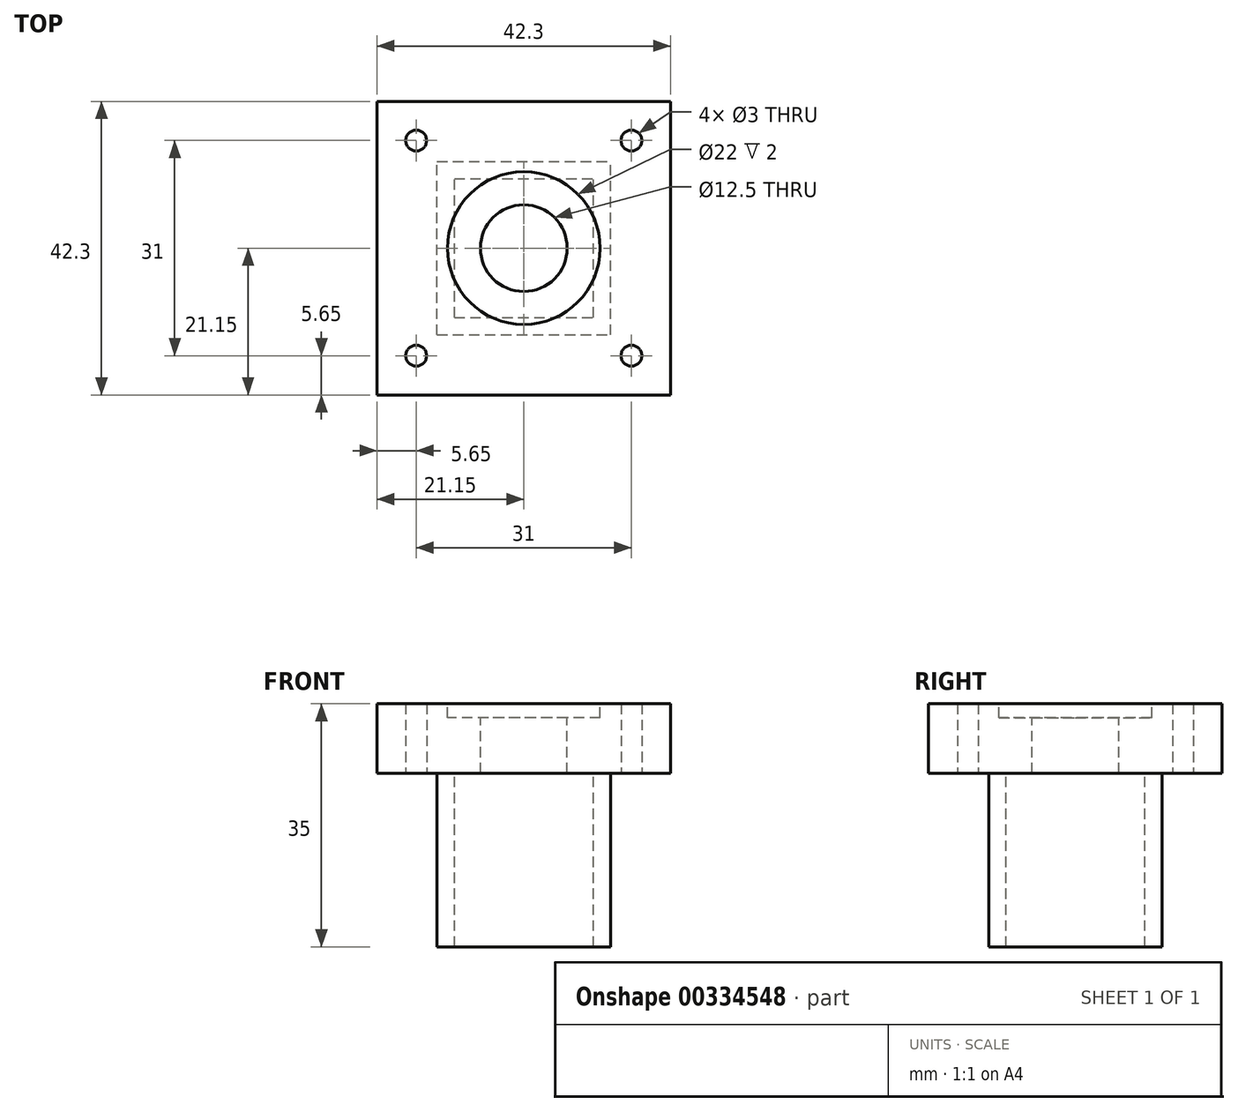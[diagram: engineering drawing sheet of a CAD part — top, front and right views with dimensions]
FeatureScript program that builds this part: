
annotation { "Feature Type Name" : "Feature", "Feature Type Description" : "" }
export const myFeature = defineFeature(function(context is Context, id is Id, definition is map)
    precondition{}
    {
        {
            var Q0;
            Q0=qCreatedBy(makeId("Top.planeOp"),FACE);
            var sketch = newSketch(context, id + "F0", { "sketchPlane" : qUnion([Q0])});
            skLineSegment(sketch, "E0.bottom", {"start": v(21.15, -21.15) * mm, "end": v(-21.15, -21.15) * mm});
            skLineSegment(sketch, "E0.top", {"start": v(21.15, 21.15) * mm, "end": v(-21.15, 21.15) * mm});
            skLineSegment(sketch, "E0.left", {"start": v(21.15, -21.15) * mm, "end": v(21.15, 21.15) * mm});
            skLineSegment(sketch, "E0.right", {"start": v(-21.15, -21.15) * mm, "end": v(-21.15, 21.15) * mm});
            skPoint(sketch, "E0.middle", {"position": v(0, 0) * mm});
            skLineSegment(sketch, "E1.bottom", {"start": v(15.5, -15.5) * mm, "end": v(-15.5, -15.5) * mm});
            skLineSegment(sketch, "E1.top", {"start": v(15.5, 15.5) * mm, "end": v(-15.5, 15.5) * mm});
            skLineSegment(sketch, "E1.left", {"start": v(15.5, -15.5) * mm, "end": v(15.5, 15.5) * mm});
            skLineSegment(sketch, "E1.right", {"start": v(-15.5, -15.5) * mm, "end": v(-15.5, 15.5) * mm});
            skCircle(sketch, "E2", {"center": v(-15.5, 15.5) * mm, "radius": 1.5 * mm});
            skCircle(sketch, "E3", {"center": v(15.5, 15.5) * mm, "radius": 1.5 * mm});
            skCircle(sketch, "E4", {"center": v(15.5, -15.5) * mm, "radius": 1.5 * mm});
            skCircle(sketch, "E5", {"center": v(-15.5, -15.5) * mm, "radius": 1.5 * mm});
            skCircle(sketch, "E6", {"center": v(0, 0) * mm, "radius": 2.5 * mm});
            skCircle(sketch, "E7", {"center": v(0, 0) * mm, "radius": 7.5 * mm});
            skSolve(sketch);
        }
        {
            var Q0;
            Q0=makeQuery(id+"F0.imprint","IMPRINT",FACE,{"disambiguationData":[TD([[makeQuery(id+"F0.imprint","IMPRINT",EDGE,{"derivedFrom":sQuery(id+"F0.wireOp",EDGE,"E0.bottom")}),-1.0]])]});
            var Q1;
            {var subQ5=sQuery(id+"F0.wireOp",EDGE,"E4");var subQ10=sQuery(id+"F0.wireOp",EDGE,"E1.bottom");var subQ15=makeQuery(id+"F0.imprint","INTERSECT",VERTEX,{"derivedFrom":[subQ10,subQ5]});Q1=makeQuery(id+"F0.imprint","IMPRINT",FACE,{"disambiguationData":[TD([[makeQuery(id+"F0.imprint","IMPRINT",EDGE,{"disambiguationData":[TD([[subQ15,-1.0]])],"derivedFrom":subQ10}),-1.0]])]});}
            var Q2;
            Q2=makeQuery(id+"F0.imprint","IMPRINT",FACE,{"disambiguationData":[TD([[makeQuery(id+"F0.imprint","IMPRINT",EDGE,{"derivedFrom":sQuery(id+"F0.wireOp",EDGE,"E6")}),-1.0]])]});
            extrude(context, id + "F1", {"entities" : qUnion([Q0, Q1, Q2]), "depth" : 10 * mm});
        }
        {
            var Q0;
            Q0=makeQuery(id+"F1.opExtrude","CAP_FACE",FACE,{"disambiguationData":[OSD([sQuery(id+"F0.wireOp",EDGE,"E0.bottom"),sQuery(id+"F0.wireOp",EDGE,"E0.top"),sQuery(id+"F0.wireOp",EDGE,"E0.left"),sQuery(id+"F0.wireOp",EDGE,"E0.right"),sQuery(id+"F0.wireOp",EDGE,"E2"),sQuery(id+"F0.wireOp",EDGE,"E3"),sQuery(id+"F0.wireOp",EDGE,"E4"),sQuery(id+"F0.wireOp",EDGE,"E5"),sQuery(id+"F0.wireOp",EDGE,"rhQvAy9Y-mNkr-RHWF-U774-nVmRSzUEfXTO")])],"isStart":false});
            var sketch = newSketch(context, id + "F2", { "sketchPlane" : qUnion([Q0])});
            skCircle(sketch, "E8", {"center": v(0, 0) * mm, "radius": 11 * mm});
            skSolve(sketch);
        }
        {
            var Q0;
            Q0 = qSketchRegion(id + "F2", true);
            extrude(context, id + "F3", {"entities" : qUnion([Q0]), "operationType" : NewBodyOperationType.REMOVE, "oppositeDirection" : true, "depth" : 2 * mm});
        }
        {
            var Q0;
            Q0=makeQuery(id+"F1.opExtrude","CAP_FACE",FACE,{"disambiguationData":[OSD([sQuery(id+"F0.wireOp",EDGE,"E0.bottom"),sQuery(id+"F0.wireOp",EDGE,"E0.top"),sQuery(id+"F0.wireOp",EDGE,"E0.left"),sQuery(id+"F0.wireOp",EDGE,"E0.right"),sQuery(id+"F0.wireOp",EDGE,"E2"),sQuery(id+"F0.wireOp",EDGE,"E3"),sQuery(id+"F0.wireOp",EDGE,"E4"),sQuery(id+"F0.wireOp",EDGE,"E5"),sQuery(id+"F0.wireOp",EDGE,"E6")])],"isStart":true});
            var sketch = newSketch(context, id + "F4", { "sketchPlane" : qUnion([Q0])});
            skLineSegment(sketch, "E9.bottom", {"start": v(-10, 10) * mm, "end": v(10, 10) * mm});
            skLineSegment(sketch, "E9.top", {"start": v(-10, -10) * mm, "end": v(10, -10) * mm});
            skLineSegment(sketch, "E9.left", {"start": v(-10, 10) * mm, "end": v(-10, -10) * mm});
            skLineSegment(sketch, "E9.right", {"start": v(10, 10) * mm, "end": v(10, -10) * mm});
            skPoint(sketch, "E9.middle", {"position": v(0, 0) * mm});
            skLineSegment(sketch, "E10.bottom", {"start": v(10, 10) * mm, "end": v(-10, 10) * mm});
            skLineSegment(sketch, "E10.top", {"start": v(10, 7.5) * mm, "end": v(-10, 7.5) * mm});
            skLineSegment(sketch, "E10.left", {"start": v(10, 10) * mm, "end": v(10, 7.5) * mm});
            skLineSegment(sketch, "E10.right", {"start": v(-10, 10) * mm, "end": v(-10, 7.5) * mm});
            skLineSegment(sketch, "E11.bottom", {"start": v(-7.5, 7.5) * mm, "end": v(7.5, 7.5) * mm});
            skLineSegment(sketch, "E11.top", {"start": v(-7.5, -7.5) * mm, "end": v(7.5, -7.5) * mm});
            skLineSegment(sketch, "E11.left", {"start": v(-7.5, 7.5) * mm, "end": v(-7.5, -7.5) * mm});
            skLineSegment(sketch, "E11.right", {"start": v(7.5, 7.5) * mm, "end": v(7.5, -7.5) * mm});
            skLineSegment(sketch, "E12.bottom", {"start": v(-12.5, 12.5) * mm, "end": v(12.5, 12.5) * mm});
            skLineSegment(sketch, "E12.top", {"start": v(-12.5, -12.5) * mm, "end": v(12.5, -12.5) * mm});
            skLineSegment(sketch, "E12.left", {"start": v(-12.5, 12.5) * mm, "end": v(-12.5, -12.5) * mm});
            skLineSegment(sketch, "E12.right", {"start": v(12.5, 12.5) * mm, "end": v(12.5, -12.5) * mm});
            skSolve(sketch);
        }
        {
            var Q0;
            Q0=makeQuery(id+"F4.imprint","IMPRINT",FACE,{"disambiguationData":[TD([[makeQuery(id+"F4.imprint","IMPRINT",EDGE,{"derivedFrom":sQuery(id+"F4.wireOp",EDGE,"E9.top")}),-1.0]])]});
            var Q1;
            Q1=makeQuery(id+"F4.imprint","IMPRINT",FACE,{"disambiguationData":[TD([[makeQuery(id+"F4.imprint","IMPRINT",EDGE,{"derivedFrom":sQuery(id+"F4.wireOp",EDGE,"E11.bottom")}),-1.0]])]});
            var Q2;
            Q2=makeQuery(id+"F4.imprint","IMPRINT",FACE,{"disambiguationData":[TD([[makeQuery(id+"F4.imprint","IMPRINT",EDGE,{"derivedFrom":sQuery(id+"F4.wireOp",EDGE,"E10.bottom")}),1.0]])]});
            extrude(context, id + "F5", {"entities" : qUnion([Q0, Q1, Q2]), "operationType" : NewBodyOperationType.ADD, "depth" : 25 * mm});
        }
        {
            var Q0;
            Q0=makeQuery(id+"F3.boolean.opBoolean","COPY",FACE,{"derivedFrom":makeQuery(id+"F3.opExtrude","CAP_FACE",FACE,{"disambiguationData":[OSD([sQuery(id+"F2.wireOp",EDGE,"E8")])],"isStart":false})});
            var sketch = newSketch(context, id + "F6", { "sketchPlane" : qUnion([Q0])});
            skCircle(sketch, "E13", {"center": v(0, 0) * mm, "radius": 6.25 * mm});
            skSolve(sketch);
        }
        {
            var Q0;
            Q0 = qSketchRegion(id + "F6", true);
            extrude(context, id + "F7", {"entities" : qUnion([Q0]), "operationType" : NewBodyOperationType.REMOVE, "oppositeDirection" : true, "depth" : 10 * mm});
        }
    });
